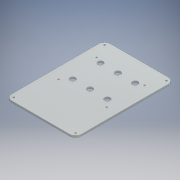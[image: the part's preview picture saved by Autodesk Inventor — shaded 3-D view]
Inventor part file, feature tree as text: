
AUTODESK INVENTOR PART (.ipt)
format: ipt  version: 2016 (Build 200138000, 138)  size: 164,864 bytes
history: native  units: mm
features: extrude x4, sketch x2, other x1, fillet x1, mirror x1, projected_geometry x1
ambient origin geometry x8: Origin, YZ Plane, XZ Plane, XY Plane, X Axis, Y Axis, Z Axis, Center Point
bodies: Solid1 (feature_tree)
feature tree (10):
  other  "FrontPanel.ipt"
  extrude  "Extrusion1"  Depth=3.0mm TaperAngle=0.0deg
  fillet  "Fillet1"  Radius=10.0mm
  sketch  "Sketch2"  dims[d4=9.925mm d5=25.0mm d6=43.0mm d7=9.925mm d8=9.925mm d9=9.925mm d10=3.0mm d11=0.0mm d12=3.0mm d13=0.0mm d14=43.0mm d15=90.0mm d16=70.0mm d17=30.0mm d18=3.016667mm d19=0.75mm d20=2.0mm d21=3.0mm d22=0.0mm]
  extrude  "Extrusion2"  Depth=3.0mm
  extrude  "Extrusion3"  Depth=3.0mm
  mirror  "Mirror1"
  extrude  "Extrusion4"  Depth=3.0mm
  sketch  "Sketch1"  dims[d0=10.0mm d1=3.0mm d2=0.0mm d3=10.0mm]
  projected_geometry  "Projected Loop1"
